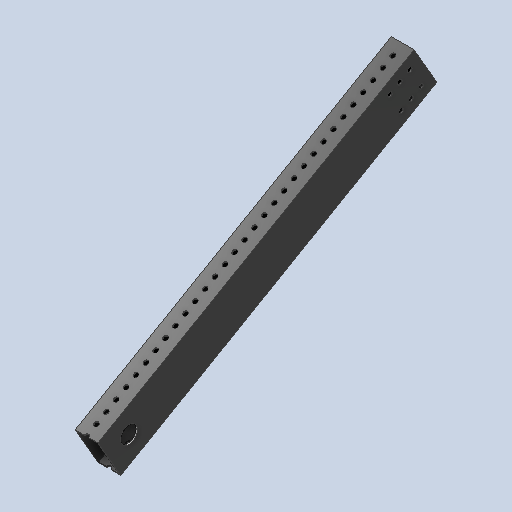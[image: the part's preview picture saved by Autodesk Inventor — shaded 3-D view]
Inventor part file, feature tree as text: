
AUTODESK INVENTOR PART (.ipt)
format: ipt  version: 2024 (Build 280153000, 153)  size: 273,408 bytes
history: native  units: in
note: dims shown in document units (in); Inventor stores cm internally (conversion verified against a paired STEP export)
features: other x4, extrude x2, sketch x2, projected_geometry x1
ambient origin geometry x8: Origin, YZ Plane, XZ Plane, XY Plane, X Axis, Y Axis, Z Axis, Center Point
bodies: Body1 (feature_tree)
feature tree (9):
  other  "2024-210-000-Angle-Shootaur.ipt"
  extrude  "Extrusion1"  Depth=0.3937in TaperAngle=0.0deg
  extrude  "Extrusion2"  Depth=1.0in
  other  "2024-210-002-Angle-Beam::2024-210-000-Angle-Shootaur.ipt"
  other  "TaggingFeature1"
  sketch  "Sketch1"  dims[d0=0.3937in d1=6.0in d2=0.0in]
  projected_geometry  "Projected Loop1"
  sketch  "Sketch2"  dims[d3=0.75in d4=1.0in d5=1.0in d6=4.625in d7=0.0in]
  other  "2024-210-002-Angle-Beam"
